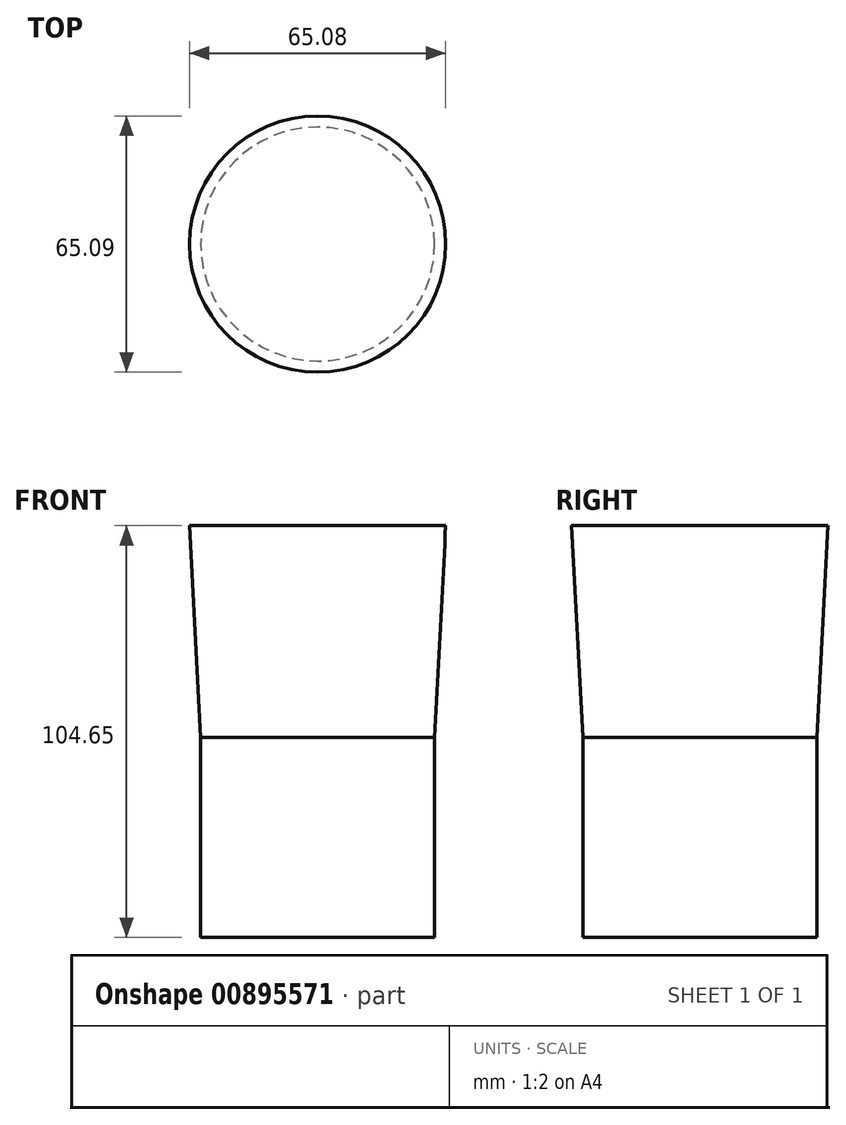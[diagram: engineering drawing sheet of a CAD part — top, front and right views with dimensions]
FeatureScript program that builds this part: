
annotation { "Feature Type Name" : "Feature", "Feature Type Description" : "" }
export const myFeature = defineFeature(function(context is Context, id is Id, definition is map)
    precondition{}
    {
        {
            var Q0;
            Q0=qCreatedBy(makeId("Top.planeOp"),FACE);
            var sketch = newSketch(context, id + "F0", { "sketchPlane" : qUnion([Q0])});
            skCircle(sketch, "E0", {"center": v(-128.69, 17.6) * mm, "radius": 29.72 * mm});
            skSolve(sketch);
        }
        {
            var Q0;
            Q0 = qSketchRegion(id + "F0", true);
            extrude(context, id + "F1", {"entities" : qUnion([Q0]), "depth" : 53.85 * mm, "offsetDistance" : 25.4 * mm, "hasDraft" : true, "draftAngle" : 3 * degree, "hasSecondDirection" : true, "secondDirectionOppositeDirection" : true, "secondDirectionDepth" : 50.8 * mm});
        }
        {
            assignVariable(context, id + "F2", {"name" : "x1", "anyValue" : 10});
        }
        {
            var Q0;
            Q0=sQuery(id+"F0.wireOp",EDGE,"E0");
            extrude(context, id + "F3", {"bodyType" : ToolBodyType.SURFACE, "surfaceEntities" : qUnion([Q0]), "depth" : (getVariable(context, 'x1')) * mm, "offsetDistance" : 25.4 * mm});
        }
    });
